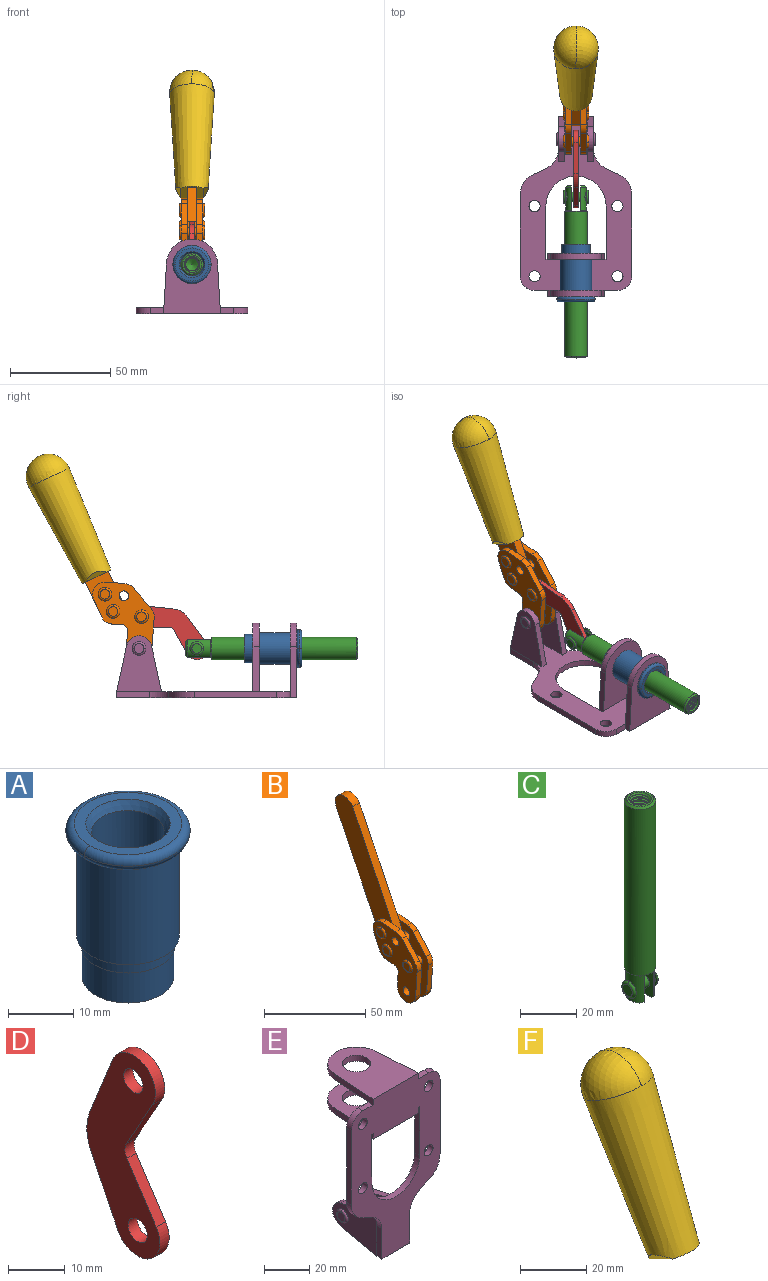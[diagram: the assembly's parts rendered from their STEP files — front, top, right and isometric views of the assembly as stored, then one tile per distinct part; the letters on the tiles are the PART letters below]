
ASSEMBLY  parts=6 mates=6
PART A: 15 faces, bbox 20.6x20.6x28.7 mm
  f0: torus R=8.26mm, axis (0,0,1), area 56.8mm2, adj f1,f10,f12
  f1: torus R=8.26mm, axis (0,0,1), area 56.8mm2, adj f0,f6,f13
  f2: cylinder r=5.59mm len=25.91mm, axis (0,0,1), area 909.6mm2, adj f3,f4
  f3: cone r=6.86mm half-angle=45deg, axis (0,0,-1), area 70.2mm2, adj f2,f14
  f4: cone r=6.47mm half-angle=30deg, axis (0,0,1), area 66.7mm2, adj f2,f13
  f5: cylinder r=7.04mm len=14.07mm, axis (0,0,1), area 252.6mm2, adj f11,f14
  f6: torus R=8.26mm, axis (0,0,1), area 56.8mm2, adj f1,f12,f13
  f7: cylinder r=7.16mm len=14.33mm, axis (0,0,1), area 91.5mm2, adj f9,f11
  f8: cylinder r=7.86mm len=18.42mm, axis (0,0,1), area 909.6mm2, adj f9,f10
  f9: plane 15.72x15.72mm, normal (0,0,-1), area 33mm2, adj f7,f8
  f10: plane 16.51x16.51mm, normal (0,0,-1), area 19.9mm2, adj f0,f8,f12
  f11: plane 14.33x14.33mm, normal (0,0,-1), area 5.7mm2, adj f5,f7
  f12: torus R=8.26mm, axis (0,0,1), area 56.8mm2, adj f0,f6,f10
  f13: plane 16.51x16.51mm, normal (0,0,1), area 82.7mm2, adj f1,f4,f6
  f14: plane 14.07x14.07mm, normal (0,0,-1), area 7.8mm2, adj f3,f5
PART B: 59 faces, bbox 12.9x60.2x99.6 mm
  f0: torus R=2.39mm, axis (-1,0,0), area 14.9mm2, adj f20,f43,f51
  f1: torus R=2.39mm, axis (-1,0,0), area 14.9mm2, adj f19,f42,f51
  f2: torus R=2.39mm, axis (-1,0,0), area 14.9mm2, adj f18,f35,f51
  f3: torus R=2.39mm, axis (-1,0,0), area 14.9mm2, adj f14,f17,f23
  f4: torus R=2.39mm, axis (-1,0,0), area 14.9mm2, adj f13,f16,f23
  f5: torus R=2.39mm, axis (-1,0,0), area 14.9mm2, adj f12,f15,f23
  f6: cylinder r=2.39mm len=4.78mm, axis (1,0,0), area 46.5mm2, adj f48,f50,f51
  f7: cylinder r=2.39mm len=4.78mm, axis (1,0,0), area 46.5mm2, adj f50,f51
  f8: cylinder r=6.35mm len=12.68mm, axis (1,0,0), area 61.8mm2, adj f38,f39,f50,f51
  f9: cylinder r=2.39mm len=4.78mm, axis (-1,0,0), area 70.5mm2, adj f46,f50
  f10: cylinder r=2.39mm len=4.78mm, axis (-1,0,0), area 46.5mm2, adj f23,f45,f46
  f11: cylinder r=2.39mm len=4.78mm, axis (-1,0,0), area 46.5mm2, adj f23,f46
  f12: plane 4.78x4.78mm, normal (1,0,0), area 17.9mm2, adj f5,f15
  f13: plane 4.78x4.78mm, normal (1,0,0), area 17.9mm2, adj f4,f16
  f14: plane 4.78x4.78mm, normal (1,0,0), area 17.9mm2, adj f3,f17
  f15: torus R=2.39mm, axis (-1,0,0), area 14.9mm2, adj f5,f12,f23
  f16: torus R=2.39mm, axis (-1,0,0), area 14.9mm2, adj f4,f13,f23
  f17: torus R=2.39mm, axis (-1,0,0), area 14.9mm2, adj f3,f14,f23
  f18: plane 4.78x4.78mm, normal (-1,0,0), area 17.9mm2, adj f2,f35
  f19: plane 4.78x4.78mm, normal (-1,0,0), area 17.9mm2, adj f1,f42
  f20: plane 4.78x4.78mm, normal (-1,0,0), area 17.9mm2, adj f0,f43
  f21: plane 2.26x0.2mm, normal (1,0,0), area 0.2mm2, adj f31,f44
  f22: plane 2.26x0.2mm, normal (-1,0,0), area 0.2mm2, adj f41,f44
  f23: plane 39.37x30.77mm, normal (1,0,0), area 565.5mm2, adj f3,f4,f5,f10,f11,f15,f16,f17
  f24: cylinder r=6.1mm len=4.15mm, axis (-1,0,0), area 14.7mm2, adj f23,f25,f32,f46
  f25: plane 10.25x9.01mm, normal (0,-0.75,0.66), area 42.3mm2, adj f23,f24,f26,f46
  f26: cylinder r=6.35mm len=4.64mm, axis (-1,0,0), area 15.6mm2, adj f23,f25,f27,f46
  f27: plane 15.84x3.1mm, normal (0,-1,-0.07), area 49.2mm2, adj f23,f26,f28,f46
  f28: cylinder r=6.35mm len=12.68mm, axis (-1,0,0), area 61.8mm2, adj f23,f27,f29,f46
  f29: plane 8.11x3.1mm, normal (0,1,0.07), area 25.2mm2, adj f23,f28,f30,f46
  f30: cylinder r=3.05mm len=3.25mm, axis (-1,0,0), area 14.8mm2, adj f23,f29,f31,f46
  f31: plane 5.99x3.1mm, normal (0,0.07,-1), area 18.6mm2, adj f21,f23,f30,f44,f46
  f32: plane 9.5x3.1mm, normal (0,-0.07,1), area 29.5mm2, adj f23,f24,f33,f46,f47
  f33: cylinder r=6.1mm len=8.63mm, axis (-1,0,0), area 39.1mm2, adj f23,f32,f34,f47
  f34: plane 8.65x3.96mm, normal (0,0.91,-0.42), area 29.5mm2, adj f23,f33,f44,f47
  f35: torus R=2.39mm, axis (-1,0,0), area 14.9mm2, adj f2,f18,f51
  f36: plane 10.25x9.01mm, normal (0,-0.75,0.66), area 42.3mm2, adj f37,f49,f50,f51
  f37: cylinder r=6.35mm len=4.64mm, axis (1,0,0), area 15.6mm2, adj f36,f38,f50,f51
  f38: plane 15.84x3.1mm, normal (0,-1,-0.07), area 49.2mm2, adj f8,f37,f50,f51
  f39: plane 8.11x3.1mm, normal (0,1,0.07), area 25.2mm2, adj f8,f40,f50,f51
  f40: cylinder r=3.05mm len=3.25mm, axis (1,0,0), area 14.8mm2, adj f39,f41,f50,f51
  f41: plane 5.99x3.1mm, normal (0,0.07,-1), area 18.6mm2, adj f22,f40,f44,f50,f51
  f42: torus R=2.39mm, axis (-1,0,0), area 14.9mm2, adj f1,f19,f51
  f43: torus R=2.39mm, axis (-1,0,0), area 14.9mm2, adj f0,f20,f51
  f44: cylinder r=6.35mm len=12.12mm, axis (-1,0,0), area 128.9mm2, adj f21,f22,f23,f31,f34,f41,f46,f47
  f45: plane 2.65x1.35mm, normal (1,0,0), area 1mm2, adj f10,f55
  f46: plane 39.08x20.42mm, normal (-1,0,0), area 412.5mm2, adj f9,f10,f11,f24,f25,f26,f27,f28
  f47: plane 77.62x39.82mm, normal (1,0,0), area 850mm2, adj f32,f33,f34,f44,f53,f54,f55
  f48: plane 2.65x1.35mm, normal (-1,0,0), area 1mm2, adj f6,f55
  f49: cylinder r=6.1mm len=4.15mm, axis (1,0,0), area 14.7mm2, adj f36,f50,f51,f56
  f50: plane 39.08x20.42mm, normal (1,0,0), area 412.5mm2, adj f6,f7,f8,f9,f36,f37,f38,f39
  f51: plane 39.37x30.77mm, normal (-1,0,0), area 565.5mm2, adj f0,f1,f2,f6,f7,f8,f35,f36
  f52: plane 8.65x3.96mm, normal (0,0.91,-0.42), area 29.5mm2, adj f44,f51,f57,f58
  f53: plane 68.49x33.4mm, normal (0,0.9,-0.44), area 358.1mm2, adj f44,f47,f54,f58
  f54: cylinder r=6.35mm len=12.06mm, axis (1,0,0), area 93.7mm2, adj f47,f53,f55,f58
  f55: plane 68.49x33.4mm, normal (0,-0.9,0.44), area 358.1mm2, adj f44,f45,f46,f47,f48,f50,f54,f58
  f56: plane 9.5x3.1mm, normal (0,-0.07,1), area 29.5mm2, adj f49,f50,f51,f57,f58
  f57: cylinder r=6.1mm len=8.63mm, axis (1,0,0), area 39.1mm2, adj f51,f52,f56,f58
  f58: plane 77.62x39.82mm, normal (-1,0,0), area 850mm2, adj f44,f52,f53,f54,f55,f56,f57
PART C: 48 faces, bbox 12.6x11.1x86.1 mm
  f0: torus R=2.41mm, axis (-1,0,0), area 15mm2, adj f30,f32,f34
  f1: torus R=2.41mm, axis (-1,0,0), area 15mm2, adj f29,f31,f33
  f2: cylinder r=5.54mm len=72.39mm, axis (0,0,1), area 2518.5mm2, adj f3,f4,f42,f43
  f3: cone r=5.54mm half-angle=45deg, axis (0,0,1), area 7.6mm2, adj f2,f5,f41
  f4: cone r=5.54mm half-angle=45deg, axis (0,0,-1), area 34.9mm2, adj f2,f39
  f5: cylinder r=5.08mm len=11.48mm, axis (0,0,1), area 108.3mm2, adj f3,f7,f8,f41
  f6: cylinder r=2.41mm len=4.83mm, axis (-1,0,0), area 71.2mm2, adj f40,f41
  f7: cylinder r=2.41mm len=4.83mm, axis (-1,0,0), area 7.6mm2, adj f5,f34
  f8: cone r=5.08mm half-angle=45deg, axis (0,0,1), area 10.6mm2, adj f5,f37,f41
  f9: cone r=3.98mm half-angle=45deg, axis (0,0,1), area 17.6mm2, adj f27,f39,f45,f46,f47
  f10: cylinder r=2.41mm len=4.83mm, axis (-1,0,0), area 7.6mm2, adj f33,f38
  f11: cylinder r=3.2mm len=6.4mm, axis (0,0,1), area 78.4mm2, adj f12,f28,f44,f45,f47
  f12: cylinder r=3.2mm len=6.4mm, axis (0,0,1), area 10.5mm2, adj f11,f13,f45,f47
  f13: cylinder r=3.2mm len=6.4mm, axis (0,0,1), area 10.5mm2, adj f12,f14,f45,f47
  f14: cylinder r=3.2mm len=6.4mm, axis (0,0,1), area 10.5mm2, adj f13,f15,f45,f47
  f15: cylinder r=3.2mm len=6.4mm, axis (0,0,1), area 10.5mm2, adj f14,f16,f45,f47
  f16: cylinder r=3.2mm len=6.4mm, axis (0,0,1), area 10.5mm2, adj f15,f17,f45,f47
  f17: cylinder r=3.2mm len=6.4mm, axis (0,0,1), area 10.5mm2, adj f16,f18,f45,f47
  f18: cylinder r=3.2mm len=6.4mm, axis (0,0,1), area 10.5mm2, adj f17,f19,f45,f47
  f19: cylinder r=3.2mm len=6.4mm, axis (0,0,1), area 10.5mm2, adj f18,f20,f45,f47
  f20: cylinder r=3.2mm len=6.4mm, axis (0,0,1), area 10.5mm2, adj f19,f21,f45,f47
  f21: cylinder r=3.2mm len=6.4mm, axis (0,0,1), area 10.5mm2, adj f20,f22,f45,f47
  f22: cylinder r=3.2mm len=6.4mm, axis (0,0,1), area 10.5mm2, adj f21,f23,f45,f47
  f23: cylinder r=3.2mm len=6.4mm, axis (0,0,1), area 10.5mm2, adj f22,f24,f45,f47
  f24: cylinder r=3.2mm len=6.4mm, axis (0,0,1), area 10.5mm2, adj f23,f25,f45,f47
  f25: cylinder r=3.2mm len=6.4mm, axis (0,0,1), area 10.5mm2, adj f24,f26,f45,f47
  f26: cylinder r=3.2mm len=6.4mm, axis (0,0,1), area 10.5mm2, adj f25,f27,f45,f47
  f27: cylinder r=3.2mm len=6.4mm, axis (0,0,1), area 7.4mm2, adj f9,f26,f45,f47
  f28: cone r=3.2mm half-angle=60deg, axis (0,0,1), area 37.2mm2, adj f11
  f29: plane 4.83x4.83mm, normal (-1,0,0), area 18.3mm2, adj f1,f31
  f30: plane 4.83x4.83mm, normal (1,0,0), area 18.3mm2, adj f0,f32
  f31: torus R=2.41mm, axis (-1,0,0), area 15mm2, adj f1,f29,f33
  f32: torus R=2.41mm, axis (-1,0,0), area 15mm2, adj f0,f30,f34
  f33: plane 6.83x6.83mm, normal (1,0,0), area 18.3mm2, adj f1,f10,f31
  f34: plane 6.83x6.83mm, normal (-1,0,0), area 18.3mm2, adj f0,f7,f32
  f35: cone r=5.08mm half-angle=45deg, axis (0,0,1), area 10.6mm2, adj f36,f38,f40
  f36: plane 7.25x1.97mm, normal (0,0,-1), area 10mm2, adj f35,f40
  f37: plane 7.25x1.97mm, normal (0,0,-1), area 10mm2, adj f8,f41
  f38: cylinder r=5.08mm len=11.48mm, axis (0,0,1), area 108.3mm2, adj f10,f35,f40,f42
  f39: plane 9.55x9.55mm, normal (0,0,1), area 22mm2, adj f4,f9
  f40: plane 12.76x10.09mm, normal (1,0,0), area 95.7mm2, adj f6,f35,f36,f38,f42,f43
  f41: plane 12.76x10.09mm, normal (-1,0,0), area 95.7mm2, adj f3,f5,f6,f8,f37,f43
  f42: cone r=5.54mm half-angle=45deg, axis (0,0,1), area 7.6mm2, adj f2,f38,f40
  f43: plane 11.07x4.7mm, normal (0,0,-1), area 50.4mm2, adj f2,f40,f41
  f44: plane 0.89x0.62mm, normal (-1,0,0), area 0.3mm2, adj f11,f45,f46,f47
  f45: bspline ~24.8x7.63mm, area 266.6mm2, adj f9,f11,f12,f13,f14,f15,f16,f17
  f46: bspline ~24.87x7.63mm, area 73.6mm2, adj f9,f44,f45,f47
  f47: bspline ~24.98x7.63mm, area 272.5mm2, adj f9,f11,f12,f13,f14,f15,f16,f17
PART D: 12 faces, bbox 2.3x18.2x42.8 mm
  f0: cylinder r=2.4mm len=4.8mm, axis (1,0,0), area 34.9mm2, adj f4,f11
  f1: cylinder r=10.41mm len=8.47mm, axis (1,0,0), area 20.2mm2, adj f4,f9,f10,f11
  f2: cylinder r=3.05mm len=3.16mm, axis (1,0,0), area 7.7mm2, adj f4,f6,f7,f11
  f3: cylinder r=2.4mm len=4.8mm, axis (1,0,0), area 34.9mm2, adj f4,f11
  f4: plane 42.81x18.23mm, normal (-1,0,0), area 414.1mm2, adj f0,f1,f2,f3,f5,f6,f7,f8
  f5: cylinder r=5.54mm len=10.67mm, axis (1,0,0), area 41.8mm2, adj f4,f6,f10,f11
  f6: plane 11.66x6.53mm, normal (0,-0.87,-0.49), area 30.9mm2, adj f2,f4,f5,f11
  f7: plane 11.17x7.33mm, normal (0,-0.84,0.55), area 30.9mm2, adj f2,f4,f8,f11
  f8: cylinder r=5.54mm len=10.51mm, axis (1,0,0), area 41.8mm2, adj f4,f7,f9,f11
  f9: plane 13.67x6.67mm, normal (0,0.9,-0.44), area 35.1mm2, adj f1,f4,f8,f11
  f10: plane 14.1x5.7mm, normal (0,0.93,0.37), area 35.1mm2, adj f1,f4,f5,f11
  f11: plane 42.81x18.23mm, normal (1,0,0), area 414.1mm2, adj f0,f1,f2,f3,f5,f6,f7,f8
PART E: 55 faces, bbox 55.7x37.4x89.8 mm
  f0: torus R=2.41mm, axis (-1,0,0), area 15mm2, adj f11,f15,f25
  f1: torus R=2.41mm, axis (-1,0,0), area 15mm2, adj f10,f12,f22
  f2: cylinder r=2.78mm len=5.56mm, axis (0,-1,0), area 54.2mm2, adj f30,f54
  f3: cylinder r=14.99mm len=29.97mm, axis (0,-1,0), area 145.9mm2, adj f30,f49,f53,f54
  f4: cylinder r=2.78mm len=5.56mm, axis (0,-1,0), area 54.2mm2, adj f30,f54
  f5: cylinder r=2.78mm len=5.56mm, axis (0,-1,0), area 54.2mm2, adj f30,f54
  f6: cylinder r=2.78mm len=5.56mm, axis (0,-1,0), area 54.2mm2, adj f30,f54
  f7: cylinder r=6.35mm len=12.7mm, axis (0,0,1), area 123.6mm2, adj f27,f51
  f8: cylinder r=6.35mm len=12.7mm, axis (0,0,-1), area 124.7mm2, adj f21,f35
  f9: cylinder r=2.41mm len=11.18mm, axis (-1,0,0), area 169.4mm2, adj f16,f19
  f10: plane 4.83x4.83mm, normal (1,0,0), area 18.3mm2, adj f1,f12
  f11: plane 4.83x4.83mm, normal (-1,0,0), area 18.3mm2, adj f0,f15
  f12: torus R=2.41mm, axis (-1,0,0), area 15mm2, adj f1,f10,f22
  f13: cylinder r=6.35mm len=12.41mm, axis (1,0,0), area 53.4mm2, adj f18,f19,f22,f23
  f14: cylinder r=6.35mm len=12.41mm, axis (-1,0,0), area 53.4mm2, adj f16,f17,f24,f25
  f15: torus R=2.41mm, axis (-1,0,0), area 15mm2, adj f0,f11,f25
  f16: plane 27.86x22.35mm, normal (1,0,0), area 425.4mm2, adj f9,f14,f17,f24,f30
  f17: plane 22.86x4.97mm, normal (0,0.21,0.98), area 72.5mm2, adj f14,f16,f25,f30
  f18: plane 22.86x4.97mm, normal (0,0.21,0.98), area 72.5mm2, adj f13,f19,f22,f30
  f19: plane 27.86x22.35mm, normal (-1,0,0), area 425.4mm2, adj f9,f13,f18,f23,f30
  f20: cylinder r=12.7mm len=25.35mm, axis (0,0,-1), area 119.8mm2, adj f21,f34,f35,f36
  f21: plane 34.21x28.07mm, normal (0,0,-1), area 702.4mm2, adj f8,f20,f30,f34,f36
  f22: plane 27.96x22.45mm, normal (1,0,0), area 407.2mm2, adj f1,f12,f13,f18,f23,f30,f42,f43
  f23: plane 22.86x4.97mm, normal (0,0.21,-0.98), area 72.5mm2, adj f13,f19,f22,f44
  f24: plane 22.86x4.97mm, normal (0,0.21,-0.98), area 72.5mm2, adj f14,f16,f25,f44
  f25: plane 27.86x22.35mm, normal (-1,0,0), area 407.1mm2, adj f0,f14,f15,f17,f24,f30,f45,f46
  f26: plane 3.1x0.95mm, normal (0,0,-1), area 2.7mm2, adj f30,f49,f50,f54
  f27: plane 34.21x28.07mm, normal (0,0,1), area 702.4mm2, adj f7,f28,f30,f50,f52
  f28: cylinder r=12.7mm len=25.35mm, axis (0,0,1), area 118.8mm2, adj f27,f50,f51,f52
  f29: plane 3.1x0.95mm, normal (0,0,-1), area 2.7mm2, adj f30,f52,f53,f54
  f30: plane 86.54x55.63mm, normal (0,1,0), area 2362.9mm2, adj f2,f3,f4,f5,f6,f16,f17,f18
  f31: plane 40.56x3.1mm, normal (-1,0,0), area 125.7mm2, adj f30,f32,f48,f54
  f32: cylinder r=7.11mm len=7.11mm, axis (0,-1,0), area 34.6mm2, adj f30,f31,f33,f54
  f33: plane 6.67x3.1mm, normal (0,0,1), area 20.4mm2, adj f30,f32,f34,f54
  f34: plane 25.39x3.13mm, normal (-1,0.06,0), area 79.5mm2, adj f20,f21,f33,f35,f54
  f35: plane 37.31x28.45mm, normal (0,0,1), area 789.9mm2, adj f8,f20,f34,f36,f54
  f36: plane 25.39x3.13mm, normal (1,0.06,0), area 79.5mm2, adj f20,f21,f35,f37,f54
  f37: plane 6.67x3.1mm, normal (0,0,1), area 20.4mm2, adj f30,f36,f38,f54
  f38: cylinder r=7.11mm len=7.11mm, axis (0,-1,0), area 34.6mm2, adj f30,f37,f39,f54
  f39: plane 40.56x3.1mm, normal (1,0,0), area 125.7mm2, adj f30,f38,f40,f54
  f40: cylinder r=11.18mm len=10.16mm, axis (0,-1,0), area 39.5mm2, adj f30,f39,f41,f54
  f41: plane 6.09x3.1mm, normal (0.42,0,-0.91), area 20.8mm2, adj f30,f40,f42,f54
  f42: cylinder r=11.18mm len=9.41mm, axis (0,-1,0), area 37.2mm2, adj f22,f30,f41,f43,f54
  f43: plane 16.5x3.1mm, normal (1,0,0), area 51.1mm2, adj f22,f42,f44,f54
  f44: plane 17.37x3.1mm, normal (0,0,-1), area 53.8mm2, adj f23,f24,f30,f43,f45,f54
  f45: plane 16.5x3.1mm, normal (-1,0,0), area 51.1mm2, adj f25,f44,f46,f54
  f46: cylinder r=11.18mm len=9.41mm, axis (0,-1,0), area 37.2mm2, adj f25,f30,f45,f47,f54
  f47: plane 6.09x3.1mm, normal (-0.42,0,-0.91), area 20.8mm2, adj f30,f46,f48,f54
  f48: cylinder r=11.18mm len=10.16mm, axis (0,-1,0), area 39.5mm2, adj f30,f31,f47,f54
  f49: plane 26.54x3.1mm, normal (-1,0,0), area 82.3mm2, adj f3,f26,f30,f54
  f50: plane 25.39x3.1mm, normal (1,0.06,0), area 78.8mm2, adj f26,f27,f28,f51,f54
  f51: plane 37.31x28.45mm, normal (0,0,-1), area 789.9mm2, adj f7,f28,f50,f52,f54
  f52: plane 25.39x3.1mm, normal (-1,0.06,0), area 78.8mm2, adj f27,f28,f29,f51,f54
  f53: plane 26.54x3.1mm, normal (1,0,0), area 82.3mm2, adj f3,f29,f30,f54
  f54: plane 89.66x55.63mm, normal (0,-1,0), area 2678.5mm2, adj f2,f3,f4,f5,f6,f26,f29,f31
PART F: 11 faces, bbox 22.3x42.6x64.5 mm
  f0: sphere r=11.13mm, area 411.4mm2, adj f1,f8
  f1: cone r=11.11mm half-angle=3.3deg, axis (0,0.44,0.9), area 3251.8mm2, adj f0,f7,f8,f9,f10
  f2: cylinder r=6.16mm len=11.7mm, axis (1,0,0), area 89.5mm2, adj f3,f4,f5,f6
  f3: plane 60.23x36.75mm, normal (-1,0,0), area 763.6mm2, adj f2,f4,f6,f10
  f4: plane 51.37x25.05mm, normal (0,0.9,-0.44), area 264.2mm2, adj f2,f3,f5,f10
  f5: plane 60.23x36.75mm, normal (1,0,0), area 763.6mm2, adj f2,f4,f6,f10
  f6: plane 51.37x25.05mm, normal (0,-0.9,0.44), area 264.2mm2, adj f2,f3,f5,f10
  f7: plane 9.95x5.95mm, normal (0.71,-0.31,-0.64), area 25.8mm2, adj f1,f10
  f8: sphere r=11.13mm, area 411.4mm2, adj f0,f1
  f9: plane 9.95x5.95mm, normal (-0.71,-0.31,-0.64), area 25.8mm2, adj f1,f10
  f10: plane 14.27x11.38mm, normal (0,-0.44,-0.9), area 106.7mm2, adj f1,f3,f4,f5,f6,f7,f9
PLACE A rot(axis=(1,0,0),90deg) t=(0,9.43,0)mm
PLACE B rot(axis=(1,0,0),0.4deg) t=(0,16.68,56.53)mm
PLACE C rot(axis=(1,0,0),90deg) t=(0,28.25,0)mm
PLACE D rot(axis=(0,-0.52,-0.86),180deg) t=(0,38.15,11.45)mm
PLACE E rot(axis=(1,0,0),90deg) t=(0,9.43,0)mm fixed
PLACE F rot(axis=(1,0,0),0.4deg) t=(0,16.68,56.53)mm
MATE fastened F.f2 <-> B.f54  axis (1,0,0) through (0,87.33,111.81)mm
MATE revolute B.f7 <-> E.f0  axis (-1,0,0) through (0,41.52,24.61)mm
MATE revolute D.f3 <-> C.f6  axis (-1,0,0) through (0,12.78,24.61)mm
MATE revolute D.f5 <-> B.f4  axis (-1,0,0) through (0,40.3,40.44)mm
MATE slider E.f7 <-> C.f2  axis (0,-1,0) through (0,-36.96,24.61)mm
MATE fastened E.f7 <-> A.f0  axis (0,-1,0) through (0,-36.96,24.61)mm
